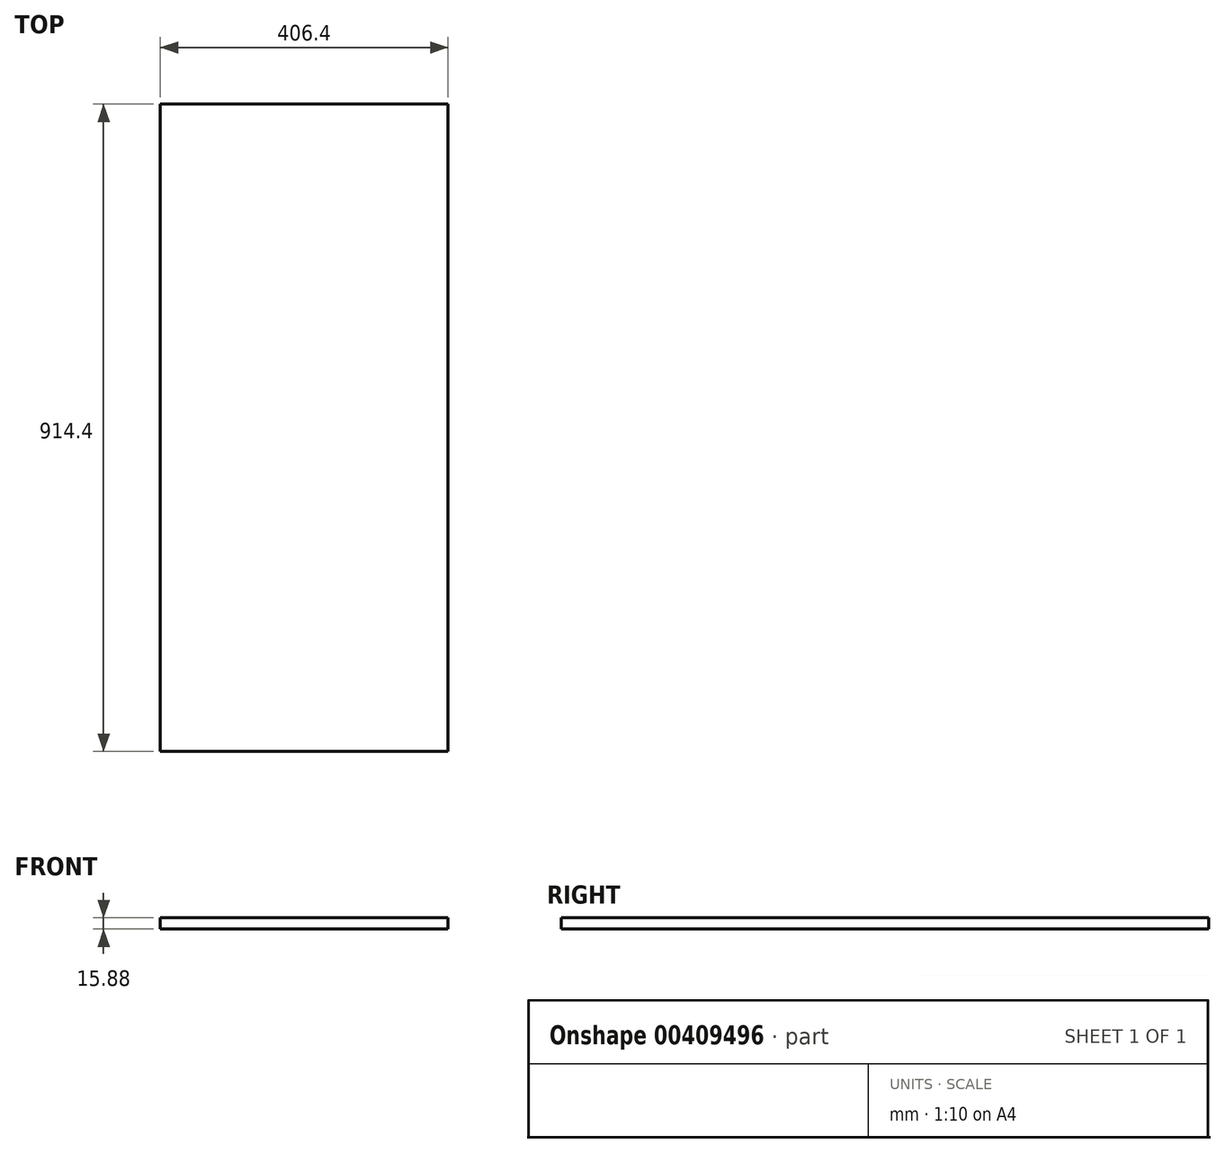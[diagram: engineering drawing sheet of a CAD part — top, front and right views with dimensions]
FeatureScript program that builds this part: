
annotation { "Feature Type Name" : "Feature", "Feature Type Description" : "" }
export const myFeature = defineFeature(function(context is Context, id is Id, definition is map)
    precondition{}
    {
        {
            var Q0;
            Q0=qCreatedBy(makeId("Front.planeOp"),FACE);
            var sketch = newSketch(context, id + "F0", { "sketchPlane" : qUnion([Q0])});
            skLineSegment(sketch, "E0.bottom", {"start": v(0, 0) * mm, "end": v(406.4, 0) * mm});
            skLineSegment(sketch, "E0.top", {"start": v(0, 15.88) * mm, "end": v(406.4, 15.88) * mm});
            skLineSegment(sketch, "E0.left", {"start": v(0, 0) * mm, "end": v(0, 15.88) * mm});
            skLineSegment(sketch, "E0.right", {"start": v(406.4, 0) * mm, "end": v(406.4, 15.88) * mm});
            skSolve(sketch);
        }
        {
            var Q0;
            Q0=makeQuery(id+"F0.imprint","IMPRINT",FACE,{"disambiguationData":[TD([[makeQuery(id+"F0.imprint","IMPRINT",EDGE,{"derivedFrom":sQuery(id+"F0.wireOp",EDGE,"E0.bottom")}),1.0]])]});
            extrude(context, id + "F1", {"entities" : qUnion([Q0]), "depth" : 914.4 * mm});
        }
    });
